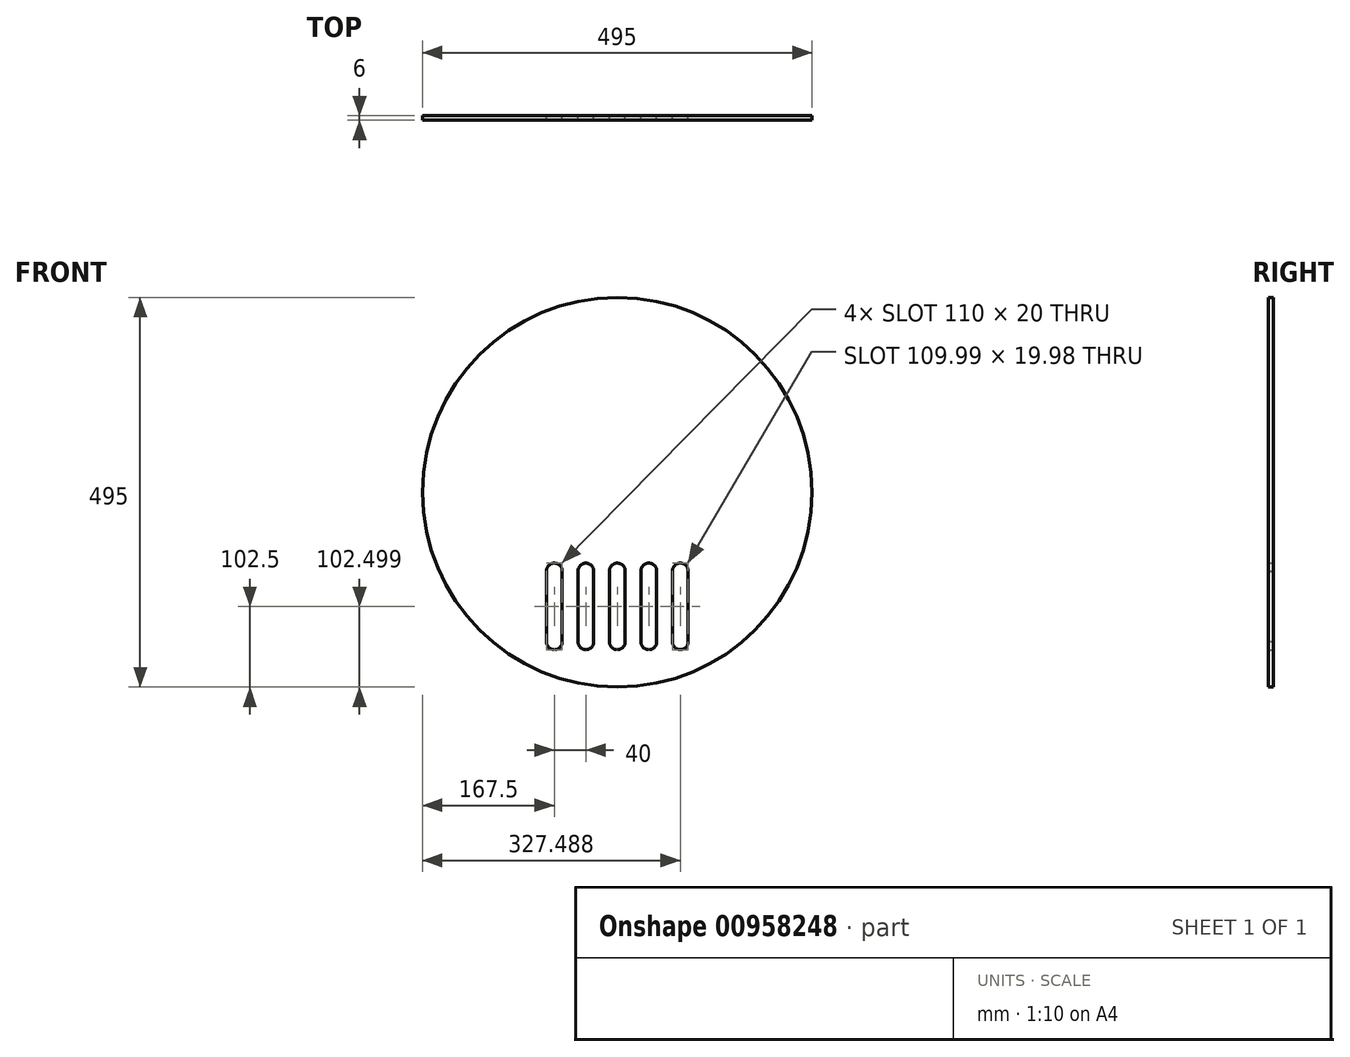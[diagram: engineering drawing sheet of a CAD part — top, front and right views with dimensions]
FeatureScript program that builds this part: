
annotation { "Feature Type Name" : "Feature", "Feature Type Description" : "" }
export const myFeature = defineFeature(function(context is Context, id is Id, definition is map)
    precondition{}
    {
        {
            var Q0;
            Q0=qCreatedBy(makeId("Front.planeOp"),FACE);
            var sketch = newSketch(context, id + "F0", { "sketchPlane" : qUnion([Q0])});
            skCircle(sketch, "E0", {"center": v(0, 0) * mm, "radius": 247.5 * mm});
            skCircle(sketch, "E1", {"center": v(-80, -100) * mm, "radius": 10 * mm});
            skCircle(sketch, "E2", {"center": v(-40, -100) * mm, "radius": 10 * mm});
            skCircle(sketch, "E3", {"center": v(0, -100) * mm, "radius": 10 * mm});
            skCircle(sketch, "E4", {"center": v(40, -100) * mm, "radius": 10 * mm});
            skCircle(sketch, "E5", {"center": v(80, -100) * mm, "radius": 10 * mm});
            skCircle(sketch, "E6", {"center": v(-80, -190) * mm, "radius": 10 * mm});
            skCircle(sketch, "E7", {"center": v(-40, -190) * mm, "radius": 10 * mm});
            skCircle(sketch, "E8", {"center": v(0, -190) * mm, "radius": 10 * mm});
            skCircle(sketch, "E9", {"center": v(40, -190) * mm, "radius": 10 * mm});
            skCircle(sketch, "E10", {"center": v(80, -190) * mm, "radius": 10 * mm});
            skLineSegment(sketch, "E11", {"start": v(-89.98, -100.66) * mm, "end": v(-90, -190) * mm});
            skLineSegment(sketch, "E12", {"start": v(-70, -100.25) * mm, "end": v(-70, -190) * mm});
            skLineSegment(sketch, "E13", {"start": v(-50, -100) * mm, "end": v(-50, -190) * mm});
            skLineSegment(sketch, "E14", {"start": v(-30, -100) * mm, "end": v(-30, -190) * mm});
            skLineSegment(sketch, "E15", {"start": v(-10, -100.24) * mm, "end": v(-10, -190.24) * mm});
            skLineSegment(sketch, "E16", {"start": v(10, -100) * mm, "end": v(10, -190) * mm});
            skLineSegment(sketch, "E17", {"start": v(30, -100.15) * mm, "end": v(30, -190) * mm});
            skLineSegment(sketch, "E18", {"start": v(50, -99.94) * mm, "end": v(50, -190) * mm});
            skLineSegment(sketch, "E19", {"start": v(70, -99.95) * mm, "end": v(70, -190.05) * mm});
            skLineSegment(sketch, "E20", {"start": v(89.98, -99.32) * mm, "end": v(89.98, -189.32) * mm});
            skSolve(sketch);
        }
        {
            var Q0;
            Q0=makeQuery(id+"F0.imprint","IMPRINT",FACE,{"disambiguationData":[TD([[makeQuery(id+"F0.imprint","IMPRINT",EDGE,{"derivedFrom":sQuery(id+"F0.wireOp",EDGE,"E0")}),1.0]])]});
            extrude(context, id + "F1", {"entities" : qUnion([Q0]), "depth" : 6 * mm, "offsetDistance" : 25.4 * mm});
        }
    });
